# Revit family: 947110001_Grifería para Lavamanos Institucional Push Pared
name_source: partatom
category: Plumbing Fixtures
units: mm (PartAtom-declared; Revit-internal decimal feet)

## family parameters
Always vertical = Yes
Cut with Voids When Loaded = No
OmniClass Number = 23.21.21.19
OmniClass Title = Commercial Dishwasher Equipment
Part Type = Normal
Room Calculation Point = No
Round Connector Dimension = Use Diameter
Shared = No
Work Plane-Based = No

## types (1)
- 947110001_Grifería para Lavamanos Institucional Push Pared
    Acabado = Cromado
    Alto = 6.3 cm
    Ancho = 6.3 cm
    Capacidad de flujo = 9.68 l/m máximo a 80 PSI
    Colección = Griferia 2016
    Consumo de agua = 9.68 lt
    Creado por = IDD
    Description = Un producto perfecto para las necesidades de las instituciones de alto tráfico al estar diseñadas para un óptimo funcionamiento y durabilidad. Destacan por sus características antivandálicas y cierre automático temporizado entre 5 a 9 segundos. Con instalación a pared tipo push antivandálica. ¡No esperes más para tenerla!
    Fecha de creación = 30/07/2020
    Garantía = 3 años
    Garantías de otros componentes = 2 años en acabados
    Incluye = Cuerpo, botón, escudo, portaescudo
    Largo = 16 cm
    Línea = Push Pared
    Material = Corona_Cromado
    Materiales = Metal
    Productos compatibles = Lavamanos Institucionales Corona
    Rango de presión de agua = Entre 20 y 80 PSI
    Resistencia = Resistente a la corrosión pelado y decoloración por agua
    Sistema antivandálico = Producto que dificulta las acciones vandálicas
    Sistema de accionamiento = Tipo push
    Tipo de grifería = De pared
    Tipo de instalación = A pared
    Tipo de manija/accionamiento = Push
    URL = https://corona.co
    Uso = Institucional

## geometry (parser evidence)
native form markers: Sweep x5
no freeform markers — native parametric forms only
